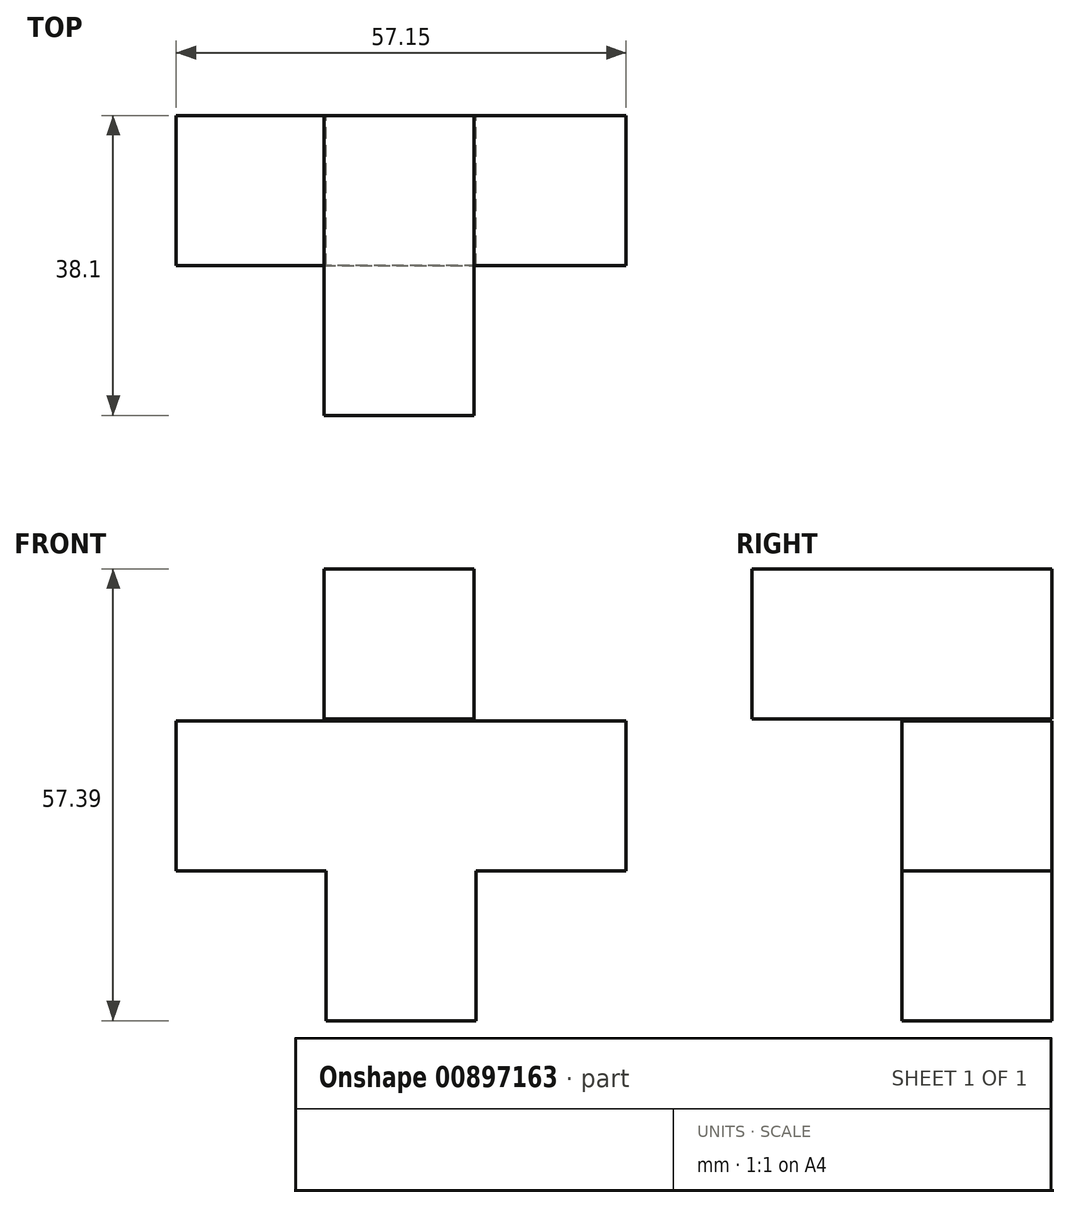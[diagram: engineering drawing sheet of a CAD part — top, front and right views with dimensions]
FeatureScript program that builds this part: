
annotation { "Feature Type Name" : "Feature", "Feature Type Description" : "" }
export const myFeature = defineFeature(function(context is Context, id is Id, definition is map)
    precondition{}
    {
        {
            var Q0;
            Q0=qCreatedBy(makeId("Front.planeOp"),FACE);
            var sketch = newSketch(context, id + "F0", { "sketchPlane" : qUnion([Q0])});
            skLineSegment(sketch, "E0", {"start": v(-33.72, 43.71) * mm, "end": v(-14.67, 43.71) * mm});
            skLineSegment(sketch, "E1", {"start": v(-14.67, 43.71) * mm, "end": v(-14.67, 24.66) * mm});
            skLineSegment(sketch, "E2", {"start": v(-33.72, 43.71) * mm, "end": v(-33.72, 24.66) * mm});
            skLineSegment(sketch, "E3", {"start": v(-33.72, 24.66) * mm, "end": v(-14.67, 24.66) * mm});
            skLineSegment(sketch, "E4", {"start": v(-14.67, 43.71) * mm, "end": v(4.38, 43.71) * mm});
            skLineSegment(sketch, "E5", {"start": v(4.38, 43.71) * mm, "end": v(4.38, 24.66) * mm});
            skLineSegment(sketch, "E6", {"start": v(-14.67, 24.66) * mm, "end": v(4.38, 24.66) * mm});
            skLineSegment(sketch, "E7", {"start": v(4.38, 24.66) * mm, "end": v(23.43, 24.66) * mm});
            skLineSegment(sketch, "E8", {"start": v(23.43, 24.66) * mm, "end": v(23.43, 43.71) * mm});
            skLineSegment(sketch, "E9", {"start": v(23.43, 43.71) * mm, "end": v(4.38, 43.71) * mm});
            skLineSegment(sketch, "E10", {"start": v(4.38, 24.66) * mm, "end": v(4.38, 5.61) * mm});
            skLineSegment(sketch, "E11", {"start": v(4.38, 5.61) * mm, "end": v(-14.67, 5.61) * mm});
            skLineSegment(sketch, "E12", {"start": v(-14.67, 24.66) * mm, "end": v(-14.67, 5.61) * mm});
            skSolve(sketch);
        }
        {
            var Q0;
            Q0=qCreatedBy(makeId("Front.planeOp"),FACE);
            var sketch = newSketch(context, id + "F1", { "sketchPlane" : qUnion([Q0])});
            skLineSegment(sketch, "E13", {"start": v(-14.95, 43.95) * mm, "end": v(-14.95, 63) * mm});
            skLineSegment(sketch, "E14", {"start": v(-14.95, 63) * mm, "end": v(4.1, 63) * mm});
            skLineSegment(sketch, "E15", {"start": v(4.1, 63) * mm, "end": v(4.1, 43.95) * mm});
            skLineSegment(sketch, "E16", {"start": v(-14.95, 43.95) * mm, "end": v(4.1, 43.95) * mm});
            skSolve(sketch);
        }
        {
            var Q0;
            Q0 = qSketchRegion(id + "F0", true);
            extrude(context, id + "F2", {"entities" : qUnion([Q0]), "depth" : 19.05 * mm, "offsetDistance" : 25.4 * mm});
        }
        {
            var Q0;
            Q0 = qSketchRegion(id + "F1", true);
            extrude(context, id + "F3", {"entities" : qUnion([Q0]), "depth" : 38.1 * mm, "offsetDistance" : 25.4 * mm});
        }
    });
